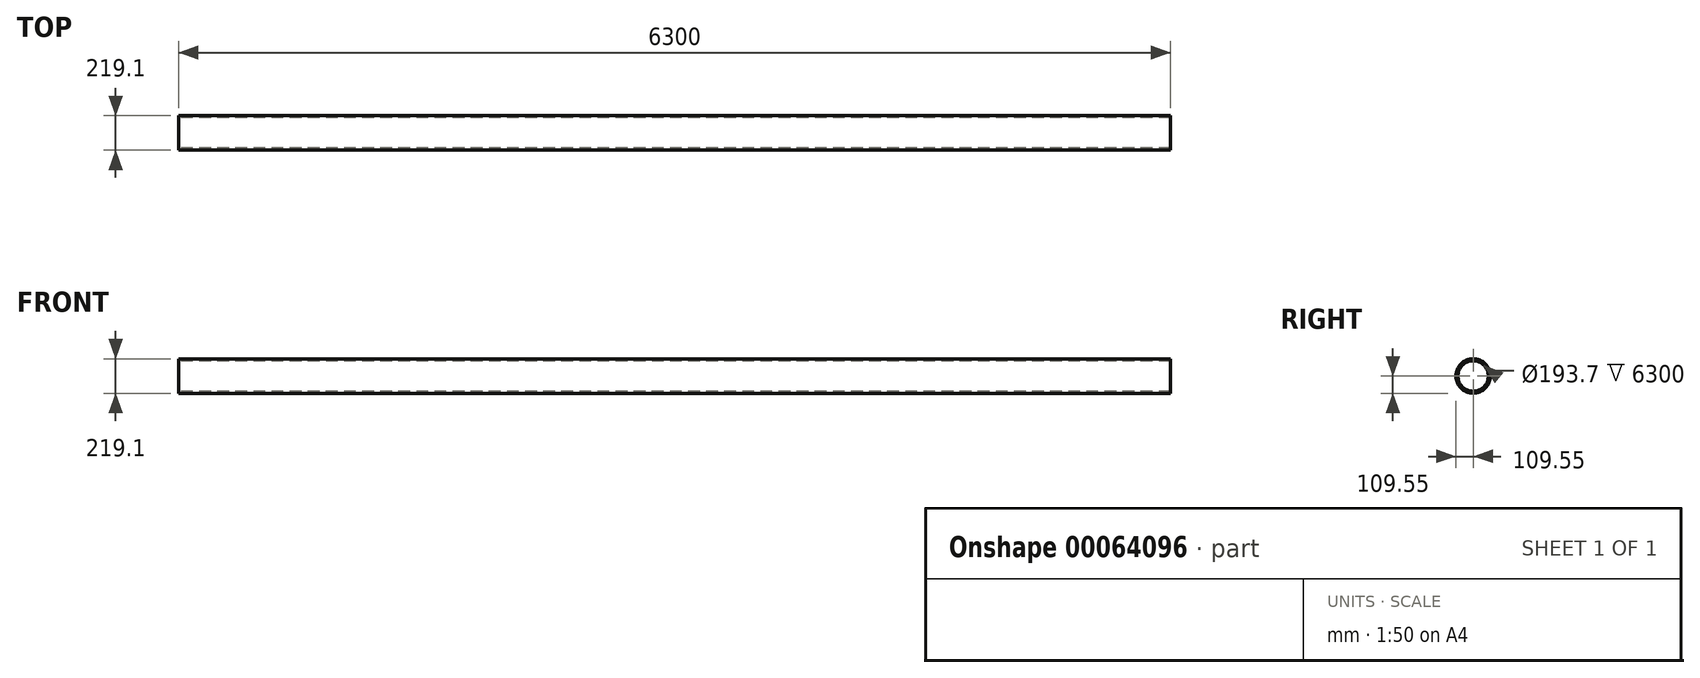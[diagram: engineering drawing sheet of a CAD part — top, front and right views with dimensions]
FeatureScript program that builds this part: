
annotation { "Feature Type Name" : "Feature", "Feature Type Description" : "" }
export const myFeature = defineFeature(function(context is Context, id is Id, definition is map)
    precondition{}
    {
        {
            var Q0;
            Q0=qCreatedBy(makeId("Right.planeOp"),FACE);
            var sketch = newSketch(context, id + "F0", { "sketchPlane" : qUnion([Q0])});
            skCircle(sketch, "E0", {"center": v(0, 0) * mm, "radius": 109.55 * mm});
            skCircle(sketch, "E1", {"center": v(0, 0) * mm, "radius": 96.85 * mm});
            skSolve(sketch);
        }
        {
            var Q0;
            Q0=makeQuery(id+"F0.imprint","IMPRINT",FACE,{"disambiguationData":[TD([[makeQuery(id+"F0.imprint","IMPRINT",EDGE,{"derivedFrom":sQuery(id+"F0.wireOp",EDGE,"E0")}),1.0]])]});
            extrude(context, id + "F1", {"entities" : qUnion([Q0]), "endBound" : BoundingType.SYMMETRIC, "depth" : 6300 * mm});
        }
    });
